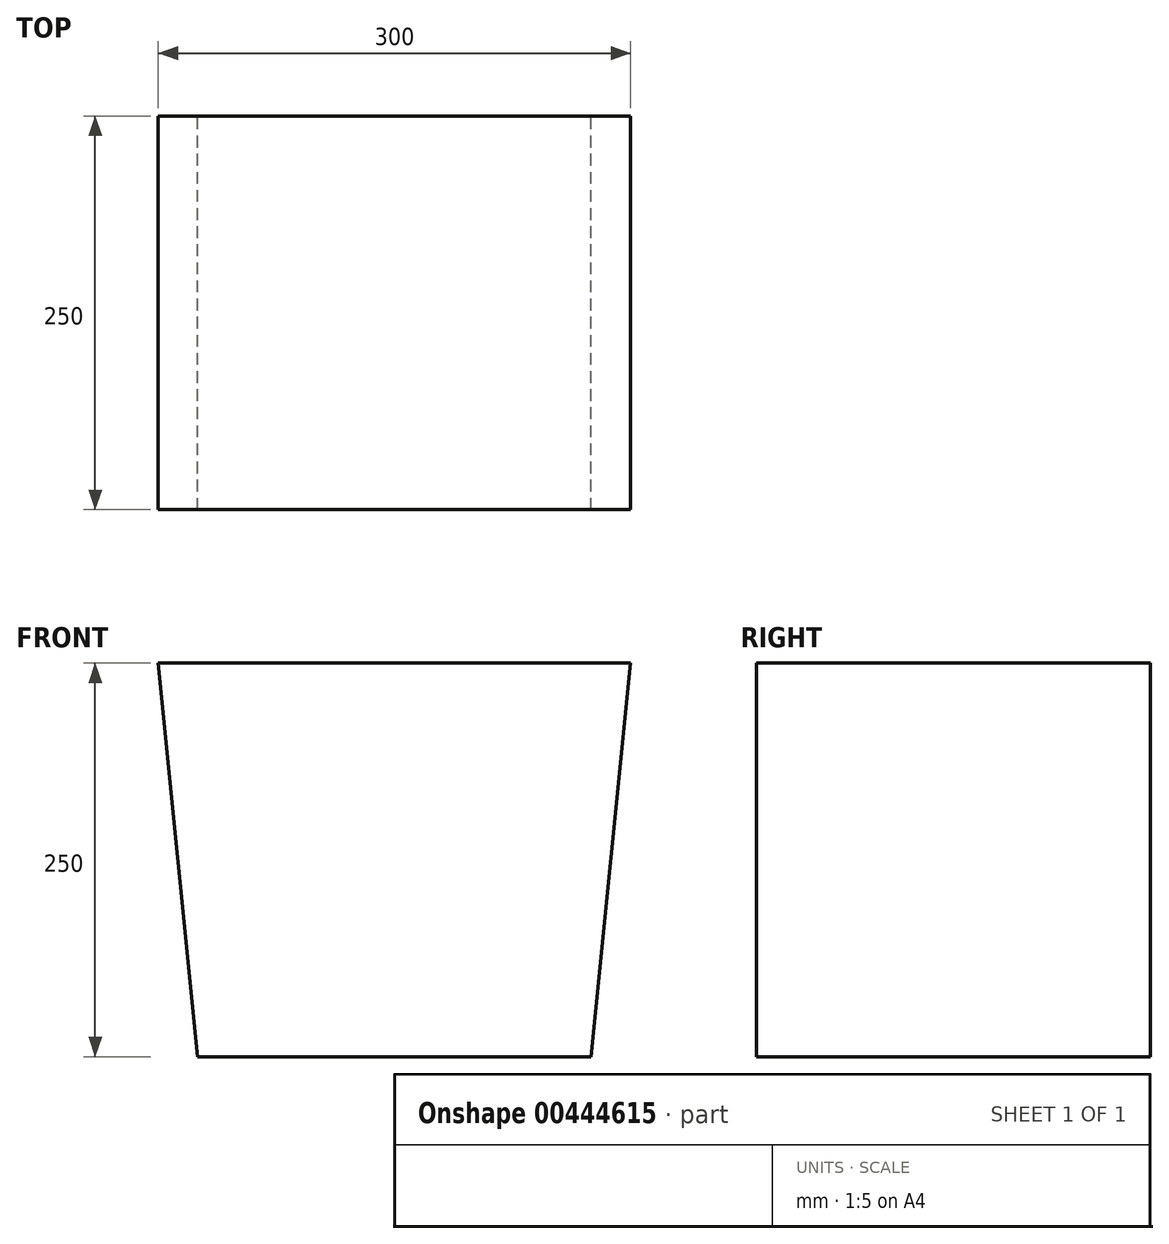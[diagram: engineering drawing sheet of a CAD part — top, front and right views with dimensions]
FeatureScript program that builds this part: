
annotation { "Feature Type Name" : "Feature", "Feature Type Description" : "" }
export const myFeature = defineFeature(function(context is Context, id is Id, definition is map)
    precondition{}
    {
        {
            var Q0;
            Q0=qCreatedBy(makeId("Top.planeOp"),FACE);
            cPlane(context, id + "F0", {"entities" : qUnion([Q0]), "cplaneType" : CPlaneType.OFFSET, "offset" : 250 * mm, "width" : 150 * mm, "height" : 150 * mm});
        }
        {
            var Q0;
            Q0=qCreatedBy(makeId("Top.planeOp"),FACE);
            var sketch = newSketch(context, id + "F1", { "sketchPlane" : qUnion([Q0])});
            skLineSegment(sketch, "E0.bottom", {"start": v(125, -125) * mm, "end": v(-125, -125) * mm});
            skLineSegment(sketch, "E0.top", {"start": v(125, 125) * mm, "end": v(-125, 125) * mm});
            skLineSegment(sketch, "E0.left", {"start": v(125, -125) * mm, "end": v(125, 125) * mm});
            skLineSegment(sketch, "E0.right", {"start": v(-125, -125) * mm, "end": v(-125, 125) * mm});
            skPoint(sketch, "E0.middle", {"position": v(0, 0) * mm});
            skSolve(sketch);
        }
        {
            var Q0;
            Q0=qCreatedBy(id+"F0.planeOp",FACE);
            var sketch = newSketch(context, id + "F2", { "sketchPlane" : qUnion([Q0])});
            skLineSegment(sketch, "E1.bottom", {"start": v(150, -125) * mm, "end": v(-150, -125) * mm});
            skLineSegment(sketch, "E1.top", {"start": v(150, 125) * mm, "end": v(-150, 125) * mm});
            skLineSegment(sketch, "E1.left", {"start": v(150, -125) * mm, "end": v(150, 125) * mm});
            skLineSegment(sketch, "E1.right", {"start": v(-150, -125) * mm, "end": v(-150, 125) * mm});
            skPoint(sketch, "E1.middle", {"position": v(0, 0) * mm});
            skSolve(sketch);
        }
        {
            var Q0;
            Q0=makeQuery(id+"F2.imprint","IMPRINT",FACE,{"disambiguationData":[TD([[makeQuery(id+"F2.imprint","IMPRINT",EDGE,{"derivedFrom":sQuery(id+"F2.wireOp",EDGE,"E1.bottom")}),-1.0]])]});
            var Q1;
            Q1=makeQuery(id+"F1.imprint","IMPRINT",FACE,{"disambiguationData":[TD([[makeQuery(id+"F1.imprint","IMPRINT",EDGE,{"derivedFrom":sQuery(id+"F1.wireOp",EDGE,"E0.bottom")}),-1.0]])]});
            loft(context, id + "F3", {"sheetProfilesArray" : [{ "sheetProfileEntities" : qUnion([Q0]) }, { "sheetProfileEntities" : qUnion([Q1]) }]});
        }
    });
